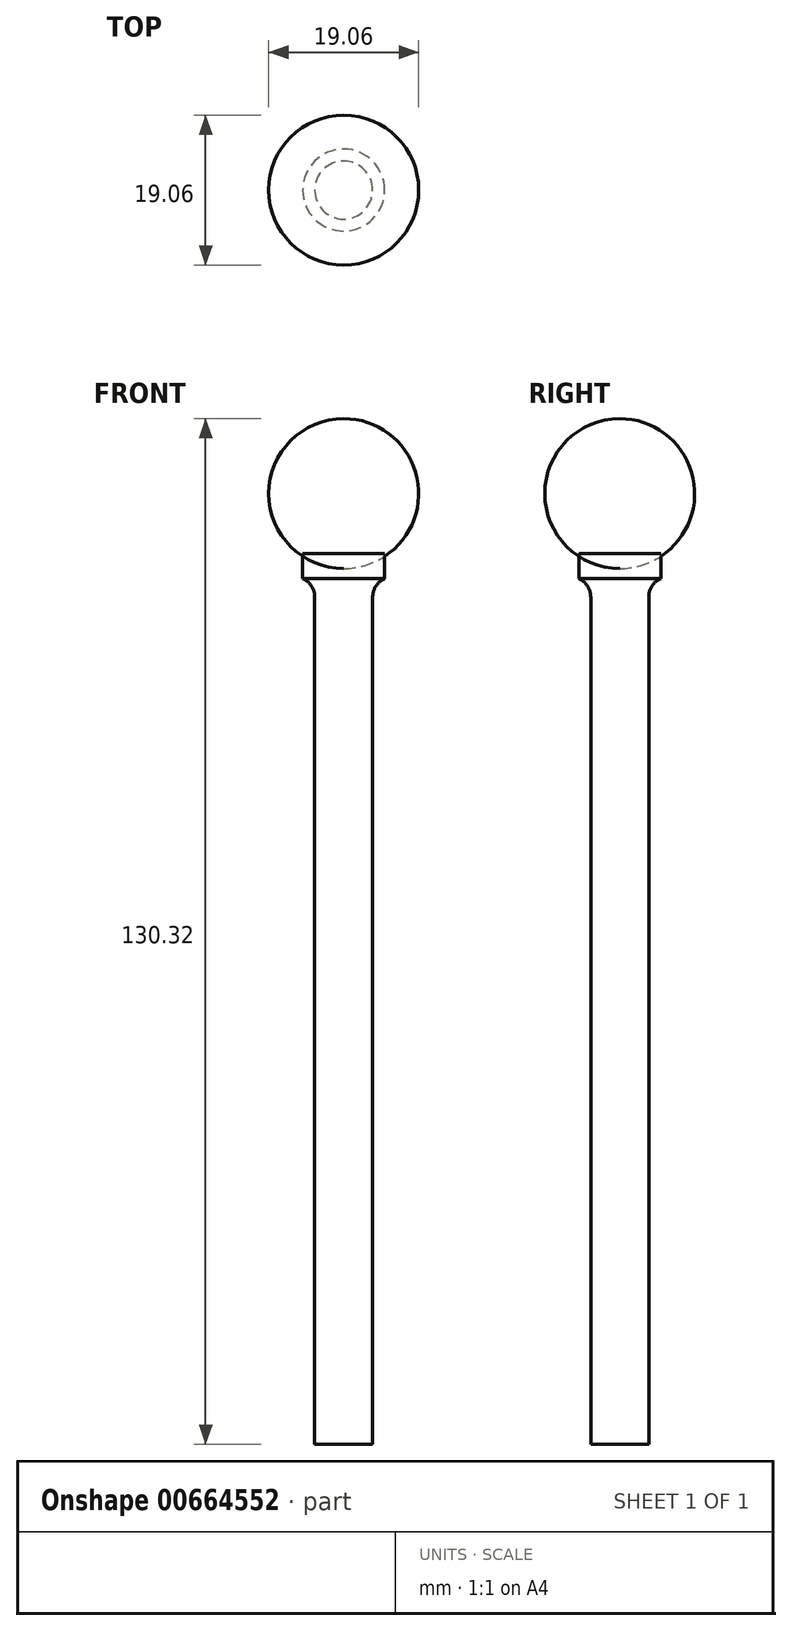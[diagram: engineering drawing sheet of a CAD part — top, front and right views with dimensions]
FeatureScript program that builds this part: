
annotation { "Feature Type Name" : "Feature", "Feature Type Description" : "" }
export const myFeature = defineFeature(function(context is Context, id is Id, definition is map)
    precondition{}
    {
        {
            var Q0;
            Q0=qCreatedBy(makeId("Front.planeOp"),FACE);
            var sketch = newSketch(context, id + "F0", { "sketchPlane" : qUnion([Q0])});
            skLineSegment(sketch, "E0", {"start": v(0, 0) * mm, "end": v(3.68, 0) * mm});
            skLineSegment(sketch, "E1", {"start": v(3.68, 0) * mm, "end": v(3.68, 110) * mm});
            skLineSegment(sketch, "E2", {"start": v(3.68, 110) * mm, "end": v(5.2, 110) * mm});
            skLineSegment(sketch, "E3", {"start": v(5.2, 110) * mm, "end": v(5.2, 113.18) * mm});
            skLineSegment(sketch, "E4", {"start": v(5.2, 113.18) * mm, "end": v(0, 113.18) * mm});
            skPoint(sketch, "E5", {"position": v(0, 113.18) * mm});
            skLineSegment(sketch, "E6", {"start": v(0, 113.18) * mm, "end": v(0, 0) * mm});
            skSolve(sketch);
        }
        {
            var Q0;
            {var subQ1=sQuery(id+"F0.wireOp",EDGE,"E0");Q0=makeQuery(id+"F0.imprint","IMPRINT",FACE,{"disambiguationData":[TD([[makeQuery(id+"F0.imprint","IMPRINT",EDGE,{"derivedFrom":subQ1}),1.0]])]});}
            var Q1;
            {var subQ0=sQuery(id+"F0.wireOp",EDGE,"E4");Q1=makeQuery(id+"F0.imprint","IMPRINT",FACE,{"disambiguationData":[TD([[makeQuery(id+"F0.imprint","IMPRINT",EDGE,{"derivedFrom":subQ0}),1.0]])]});}
            var Q2;
            Q2=sQuery(id+"F0.wireOp",EDGE,"E6");
            revolve(context, id + "F1", {"entities" : qUnion([Q0, Q1]), "axis" : qUnion([Q2]), "revolveType" : RevolveType.FULL});
        }
        {
            var Q0;
            Q0=makeQuery(id+"F1.opRevolve","SWEPT_EDGE",EDGE,{"disambiguationData":[OSD([sQuery(id+"F0.wireOp",EDGE,"E1"),sQuery(id+"F0.wireOp",EDGE,"E2")])]});
            fillet(context, id + "F2", {"entities" : qUnion([Q0]), "radius" : 2.54 * mm, "tangentPropagation" : true, "allowEdgeOverflow" : false});
        }
        {
            var Q0;
            Q0=qCreatedBy(makeId("Front.planeOp"),FACE);
            var sketch = newSketch(context, id + "F3", { "sketchPlane" : qUnion([Q0])});
            skPoint(sketch, "E7", {"position": v(0, 120.8) * mm});
            skCircle(sketch, "E8", {"center": v(0, 120.8) * mm, "radius": 9.53 * mm});
            skLineSegment(sketch, "E9", {"start": v(0, 130.32) * mm, "end": v(0, 111.27) * mm});
            skSolve(sketch);
        }
        {
            var Q0;
            {var subQ0=sQuery(id+"F3.wireOp",EDGE,"E9");Q0=makeQuery(id+"F3.imprint","IMPRINT",FACE,{"disambiguationData":[TD([[makeQuery(id+"F3.imprint","IMPRINT",EDGE,{"derivedFrom":subQ0}),1.0]])]});}
            var Q1;
            Q1=sQuery(id+"F3.wireOp",EDGE,"E9");
            revolve(context, id + "F4", {"entities" : qUnion([Q0]), "axis" : qUnion([Q1]), "revolveType" : RevolveType.FULL});
        }
    });
